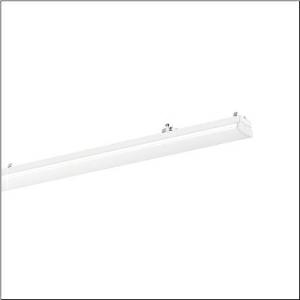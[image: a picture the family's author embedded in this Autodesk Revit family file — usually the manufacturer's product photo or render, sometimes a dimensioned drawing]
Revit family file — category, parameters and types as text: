
# Revit family: licross_21_recessed_opal_ho_52te1dcn4cxm
name_source: partatom
category: Lighting Fixtures
units: mm (PartAtom-declared; Revit-internal decimal feet)

## family parameters
Cut with Voids When Loaded = No
Host = Face
Light Source = No
Part Type = Normal
Room Calculation Point = No
Round Connector Dimension = Use Diameter
Shared = No

## types (1)
- --- (1 x LED, 12300 lm, 68.4 W, 4000K)
    Apparent Load = 68 VA
    CIE Flux Codes = 44 73 91 87 100
    Color Rendering = 80
    Color Temperature = 4000K
    Default Elevation = 1800 mm
    Description = Licross 21 recessed opal HO, luminaire insert, of sheet steel, galvanised, coil coated, white, length: 1.500mm, width: 66mm, height: 67mm, LED rated luminous flux: 12.300lm, light colour: 840, SDCM (Standard Deviation of Colour Matching)MacAdam ≤ 3 SDCM (initial), control gear: ON/OFF Multilumen, CLOi, with plug, 3-pole, with phase selection, mains connection: 220..240V, AC, 50/60Hz, start of lifetime: 68W, end of service life: 83W, internal wiring halogen-free, primary optical cover: cover, of PMMA, light emission: direct with ceiling illumination distribution, primary light characteristic: symmetric, protection rating (complete): IP54, insulation class (complete): insulation class I (protective earthing), certification: CE, ENEC, VDE, UKCA, protection symbol: D if used in an environment with non-conductive dust loads with corresponding accessories, impact resistance: IK06, permissible ambient temperature for indoor applications: -35..+30°C, corresponds to IFS (International Featured Standards) requirements for safety and quality in the food industry, reducing of maximum allowable ambient temperature of 5°C with ceiling mounting, LABS conformity tested according to VDMA 24364:2018-05, The light source and the operating device comply with the requirements of the Ecodesign Regulation (EU) 2019/2020 and are replaceable in accordance with this regulation, packaging unit: 1 piece
    Height = 83 mm
    Lamp = 1 x LED
    Lamp Light Flux = 12300 lm
    Lamp Power = 68.4 W
    Lamp count = 1
    Length = 1500 mm
    Luminous efficacy = 180 lm/W
    Manufacturer = Siteco
    ModVariant = No
    Model = 52TE1DCN4CXM
    Mounting Place = Ceiling
    Mounting Type = Pendant
    Number of Poles = 1
    OnlyDefault = Yes
    Power Factor = 1
    Product Name = Licross 21 recessed opal HO
    Product group = luminaire insert | ceiling pendant
    ProductGroupID = 901
    Protection Class = Protection class I
    Protection Degree = IP 54
    RLX_Detail_Level = 1
    RLX_Emergency_Light_Flux = 0 lm
    RLX_Emergency_Type = 0
    RLX_Emergency_Type_DB = No
    RlxData = <blob elided: 24869 chars, md5=4039cb4e>
    Socket = socket
    Standby Power = 0 W
    System Light Flux = 12300 lm
    System Power = 68 W
    Type Comments = factory setting: luminous flux: 100 % | (A | C | E) | 161 mA
    Type Image = l_1313666.jpg
    URL = http://relux.com
    VarID = @adj_075975
    Voltage = 0 V
    Weight = 0.00 kg
    Width = 76 mm

## geometry (parser evidence)
native form markers: Blend x4, Sweep x12
no freeform markers — native parametric forms only
